# Revit family: Valve-Sink_Supply-KOHLER-Complementary-K-80158IN
name_source: partatom
category: Plumbing Fixtures
units: mm (PartAtom-declared; Revit-internal decimal feet)

## family parameters
Cut with Voids When Loaded = No
Host = Face
Maintain Annotation Orientation = No
OmniClass Number = 23.27.31.00
Part Type = Normal
Room Calculation Point = No
Round Connector Dimension = Use Diameter
Shared = No

## types (6) — shared parameters
ADA Compliant = No
Assembly Code = D2020
CW Connection = Yes
Cold Water Inlet = Cold Water Inlet
Cold Water Outlet = Cold Water Outlet
Date Modified = 06/20/2024
Default Elevation = 36"
Description = Angle Valve
Flow Rate = 0 GPM
HW Connection = No
Height = 1 15/16"
Hot Water Inlet = Hot Water Inlet
Length = 3"
Manufacturer = Kohler Co.
Master Format 2014 = 23 09 13.33
Master Format 2014 Name = Control Valves
Material = Premium Metal Construction
Pressure = 0.00 psi
Product Name = Complementary
URL = https://www.kohler.co.in
Vent Connection = No
Waste Connection = No
Waste Water Outlet = Waste Water Outlet
WaterSense Certified = No
Width = 1 9/16"

## per-type parameters (varying)
| type | Finish | Model | Product Page URL | Type |
| CP-Polished Chrome | Kohler-Metal-CP-Polished_Chrome | K-80158IN-9-CP | https://www.kohler.co.in | 1 |
| AF-Vibrant French Gold | Kohler-Metal-AF-Vibrant_French_Gold | K-80158IN-9-AF | https://www.kohler.co.in | 2 |
| BN-Vibrant Brushed Nickel | Kohler-Metal-BN-Vibrant_Brushed_Nickel | K-80158IN-9-BN | https://www.kohler.co.in | 3 |
| BV-Brushed Bronze | Kohler-Metal-BV-Brushed_Bronze | K-80158IN-9-BV | https://www.kohler.co.in | 4 |
| BL-Matte Black | Kohler-Metal-BL-Matte_Black | K-80158IN-9-BL | https://www.kohler.co.in | 5 |
| 9AV, CP-Polished Chrome | Kohler-Metal-CP-Polished_Chrome | K-80158IN-9AV-CP |  | 6 |

## geometry (parser evidence)
native form markers: Sweep x5
no freeform markers — native parametric forms only
